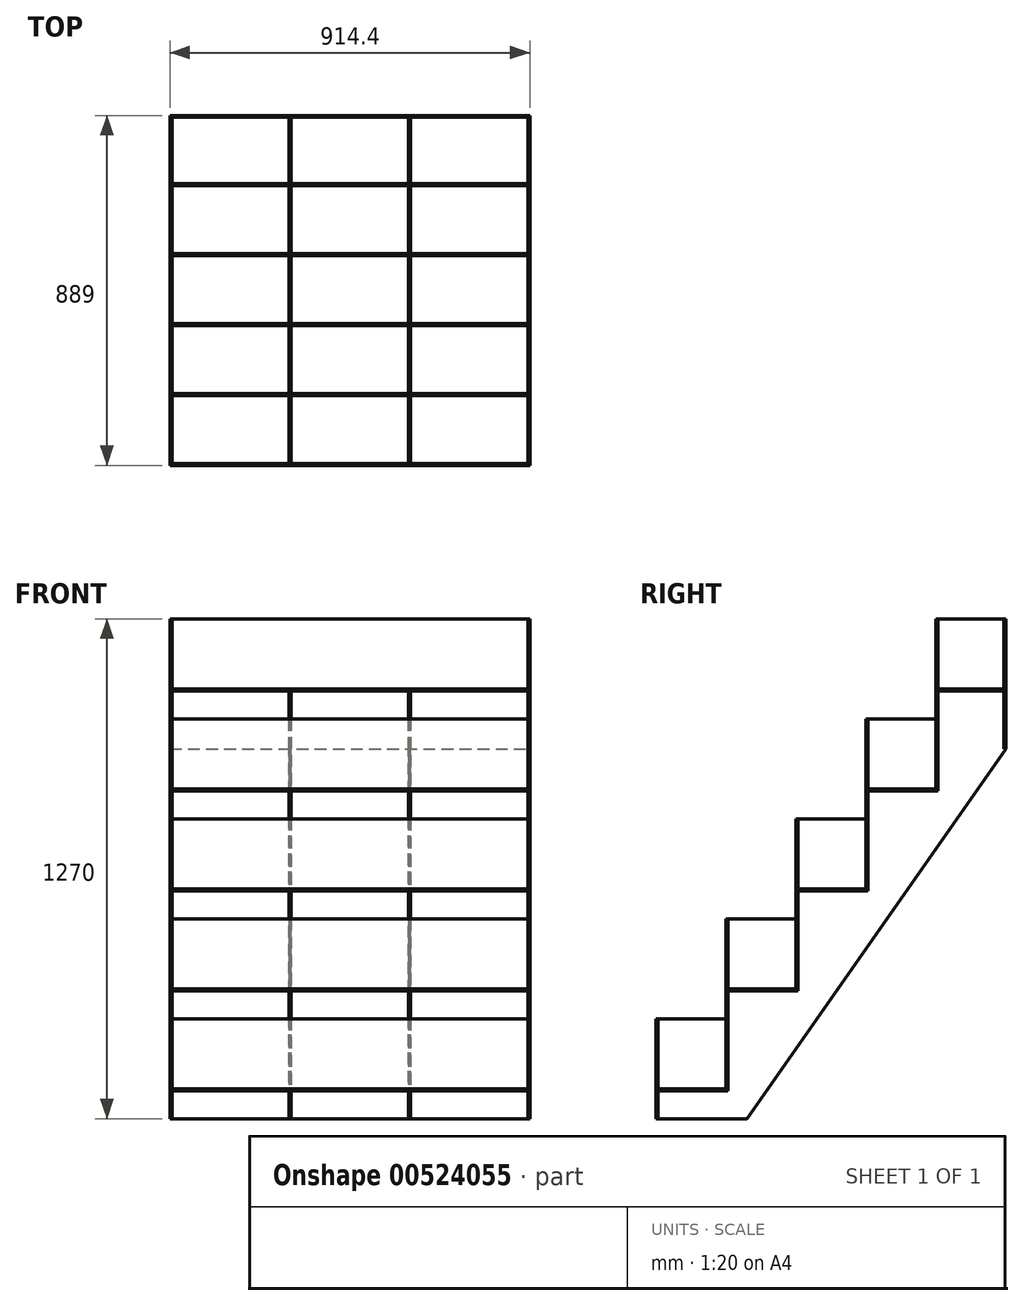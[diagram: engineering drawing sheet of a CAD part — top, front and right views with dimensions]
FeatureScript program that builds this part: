
annotation { "Feature Type Name" : "Feature", "Feature Type Description" : "" }
export const myFeature = defineFeature(function(context is Context, id is Id, definition is map)
    precondition{}
    {
        {
            assignVariable(context, id + "F0", {"name" : "matthick", "anyValue" : 5 * mm});
        }
        {
            var Q0;
            Q0=qCreatedBy(makeId("Right.planeOp"),FACE);
            var sketch = newSketch(context, id + "F1", { "sketchPlane" : qUnion([Q0])});
            skLineSegment(sketch, "E0", {"start": v(-436.82, -657.41) * mm, "end": v(-205.43, -657.41) * mm});
            skLineSegment(sketch, "E1", {"start": v(-205.43, -657.41) * mm, "end": v(452.18, 281.76) * mm});
            skLineSegment(sketch, "E2", {"start": v(452.18, 281.76) * mm, "end": v(452.18, 612.59) * mm});
            skLineSegment(sketch, "E3", {"start": v(452.18, 612.59) * mm, "end": v(274.38, 612.59) * mm});
            skLineSegment(sketch, "E4", {"start": v(274.38, 612.59) * mm, "end": v(274.38, 358.59) * mm});
            skLineSegment(sketch, "E5", {"start": v(274.38, 358.59) * mm, "end": v(96.58, 358.59) * mm});
            skLineSegment(sketch, "E6", {"start": v(96.58, 358.59) * mm, "end": v(96.58, 104.59) * mm});
            skLineSegment(sketch, "E7", {"start": v(96.58, 104.59) * mm, "end": v(-81.22, 104.59) * mm});
            skLineSegment(sketch, "E8", {"start": v(-81.22, 104.59) * mm, "end": v(-81.22, -149.41) * mm});
            skLineSegment(sketch, "E9", {"start": v(-81.22, -149.41) * mm, "end": v(-259.02, -149.41) * mm});
            skLineSegment(sketch, "E10", {"start": v(-259.02, -149.41) * mm, "end": v(-259.02, -403.41) * mm});
            skLineSegment(sketch, "E11", {"start": v(-259.02, -403.41) * mm, "end": v(-436.82, -403.41) * mm});
            skLineSegment(sketch, "E12", {"start": v(-436.82, -403.41) * mm, "end": v(-436.82, -657.41) * mm});
            skSolve(sketch);
        }
        {
            var Q0;
            Q0 = qSketchRegion(id + "F1", true);
            extrude(context, id + "F2", {"entities" : qUnion([Q0]), "depth" : getVariable(context, 'matthick'), "offsetDistance" : 25.4 * mm});
        }
        {
            var Q0;
            Q0=makeQuery(id+"F2.opExtrude","CAP_FACE",FACE,{"disambiguationData":[OSD([sQuery(id+"F1.wireOp",EDGE,"E0"),sQuery(id+"F1.wireOp",EDGE,"E1"),sQuery(id+"F1.wireOp",EDGE,"E2"),sQuery(id+"F1.wireOp",EDGE,"E3"),sQuery(id+"F1.wireOp",EDGE,"E4"),sQuery(id+"F1.wireOp",EDGE,"E5"),sQuery(id+"F1.wireOp",EDGE,"E6"),sQuery(id+"F1.wireOp",EDGE,"E7"),sQuery(id+"F1.wireOp",EDGE,"E8"),sQuery(id+"F1.wireOp",EDGE,"E9"),sQuery(id+"F1.wireOp",EDGE,"E10"),sQuery(id+"F1.wireOp",EDGE,"E11"),sQuery(id+"F1.wireOp",EDGE,"E12")])],"isStart":false});
            var sketch = newSketch(context, id + "F3", { "sketchPlane" : qUnion([Q0])});
            skLineSegment(sketch, "E13", {"start": v(274.38, 612.59) * mm, "end": v(274.38, 434.79) * mm, "construction": true});
            skLineSegment(sketch, "E14.bottom", {"start": v(274.38, 434.79) * mm, "end": v(452.18, 434.79) * mm});
            skLineSegment(sketch, "E14.top", {"start": v(274.38, 429.79) * mm, "end": v(452.18, 429.79) * mm});
            skLineSegment(sketch, "E14.left", {"start": v(274.38, 434.79) * mm, "end": v(274.38, 429.79) * mm});
            skLineSegment(sketch, "E14.right", {"start": v(452.18, 434.79) * mm, "end": v(452.18, 429.79) * mm});
            skSolve(sketch);
        }
        {
            var Q0;
            Q0=makeQuery(id+"F3.imprint","IMPRINT",FACE,{"disambiguationData":[TD([[makeQuery(id+"F3.imprint","IMPRINT",EDGE,{"derivedFrom":sQuery(id+"F3.wireOp",EDGE,"E14.bottom")}),-1.0]])]});
            extrude(context, id + "F4", {"entities" : qUnion([Q0]), "oppositeDirection" : true, "depth" : 914.4 * mm, "offsetDistance" : 25.4 * mm});
        }
        {
            var Q0;
            Q0=makeQuery(id+"F4.opExtrude","SWEPT_BODY",BODY,{"disambiguationData":[OSD([sQuery(id+"F3.wireOp",EDGE,"E14.bottom"),sQuery(id+"F3.wireOp",EDGE,"E14.top"),sQuery(id+"F3.wireOp",EDGE,"E14.left"),sQuery(id+"F3.wireOp",EDGE,"E14.right")])]});
            var Q1;
            Q1=sQuery(id+"F1.wireOp",EDGE,"E4");
            var Q2;
            Q2=sQuery(id+"F1.wireOp",EDGE,"E5");
            transform(context, id + "F5", {"entities" : qUnion([Q0]), "transformType" : TransformType.TRANSLATION_3D, "dx" : 0 * mm, "dy" : -177.8 * mm, "dz" : -254 * mm, "makeCopy" : true});
        }
        {
            var Q0;
            Q0=makeQuery(id+"F2.opExtrude","CAP_FACE",FACE,{"disambiguationData":[OSD([sQuery(id+"F1.wireOp",EDGE,"E0"),sQuery(id+"F1.wireOp",EDGE,"E1"),sQuery(id+"F1.wireOp",EDGE,"E2"),sQuery(id+"F1.wireOp",EDGE,"E3"),sQuery(id+"F1.wireOp",EDGE,"E4"),sQuery(id+"F1.wireOp",EDGE,"E5"),sQuery(id+"F1.wireOp",EDGE,"E6"),sQuery(id+"F1.wireOp",EDGE,"E7"),sQuery(id+"F1.wireOp",EDGE,"E8"),sQuery(id+"F1.wireOp",EDGE,"E9"),sQuery(id+"F1.wireOp",EDGE,"E10"),sQuery(id+"F1.wireOp",EDGE,"E11"),sQuery(id+"F1.wireOp",EDGE,"E12")])],"isStart":false});
            var sketch = newSketch(context, id + "F6", { "sketchPlane" : qUnion([Q0])});
            skLineSegment(sketch, "E15.bottom", {"start": v(274.38, 612.59) * mm, "end": v(279.38, 612.59) * mm});
            skLineSegment(sketch, "E15.top", {"start": v(274.38, 175.79) * mm, "end": v(279.38, 175.79) * mm});
            skLineSegment(sketch, "E15.left", {"start": v(274.38, 612.59) * mm, "end": v(274.38, 175.79) * mm});
            skLineSegment(sketch, "E15.right", {"start": v(279.38, 612.59) * mm, "end": v(279.38, 175.79) * mm});
            skSolve(sketch);
        }
        {
            var Q0;
            Q0 = qSketchRegion(id + "F6", true);
            extrude(context, id + "F7", {"entities" : qUnion([Q0]), "oppositeDirection" : true, "depth" : 914.4 * mm, "offsetDistance" : 25.4 * mm});
        }
        {
            var Q0;
            Q0=makeQuery(id+"F5.opPattern","COPY",BODY,{"derivedFrom":makeQuery(id+"F4.opExtrude","SWEPT_BODY",BODY,{"disambiguationData":[OSD([sQuery(id+"F3.wireOp",EDGE,"E14.bottom"),sQuery(id+"F3.wireOp",EDGE,"E14.top"),sQuery(id+"F3.wireOp",EDGE,"E14.left"),sQuery(id+"F3.wireOp",EDGE,"E14.right")])]}),"instanceName":"1"});
            var Q1;
            Q1=makeQuery(id+"F7.opExtrude","SWEPT_BODY",BODY,{"disambiguationData":[OSD([sQuery(id+"F6.wireOp",EDGE,"E15.bottom"),sQuery(id+"F6.wireOp",EDGE,"E15.top"),sQuery(id+"F6.wireOp",EDGE,"E15.left"),sQuery(id+"F6.wireOp",EDGE,"E15.right")])]});
            transform(context, id + "F8", {"entities" : qUnion([Q0, Q1]), "transformType" : TransformType.TRANSLATION_3D, "dx" : 0 * mm, "dy" : -177.8 * mm, "dz" : -254 * mm, "makeCopy" : true});
        }
        {
            var Q0;
            Q0=makeQuery(id+"F8.opPattern","COPY",BODY,{"derivedFrom":makeQuery(id+"F5.opPattern","COPY",BODY,{"derivedFrom":makeQuery(id+"F4.opExtrude","SWEPT_BODY",BODY,{"disambiguationData":[OSD([sQuery(id+"F3.wireOp",EDGE,"E14.bottom"),sQuery(id+"F3.wireOp",EDGE,"E14.top"),sQuery(id+"F3.wireOp",EDGE,"E14.left"),sQuery(id+"F3.wireOp",EDGE,"E14.right")])]}),"instanceName":"1"}),"instanceName":"1"});
            var Q1;
            Q1=makeQuery(id+"F8.opPattern","COPY",BODY,{"derivedFrom":makeQuery(id+"F7.opExtrude","SWEPT_BODY",BODY,{"disambiguationData":[OSD([sQuery(id+"F6.wireOp",EDGE,"E15.bottom"),sQuery(id+"F6.wireOp",EDGE,"E15.top"),sQuery(id+"F6.wireOp",EDGE,"E15.left"),sQuery(id+"F6.wireOp",EDGE,"E15.right")])]}),"instanceName":"1"});
            transform(context, id + "F9", {"entities" : qUnion([Q0, Q1]), "transformType" : TransformType.TRANSLATION_3D, "dx" : 0 * mm, "dy" : -177.8 * mm, "dz" : -254 * mm, "makeCopy" : true});
        }
        {
            var Q0;
            Q0=makeQuery(id+"F9.opPattern","COPY",BODY,{"derivedFrom":makeQuery(id+"F8.opPattern","COPY",BODY,{"derivedFrom":makeQuery(id+"F5.opPattern","COPY",BODY,{"derivedFrom":makeQuery(id+"F4.opExtrude","SWEPT_BODY",BODY,{"disambiguationData":[OSD([sQuery(id+"F3.wireOp",EDGE,"E14.bottom"),sQuery(id+"F3.wireOp",EDGE,"E14.top"),sQuery(id+"F3.wireOp",EDGE,"E14.left"),sQuery(id+"F3.wireOp",EDGE,"E14.right")])]}),"instanceName":"1"}),"instanceName":"1"}),"instanceName":"1"});
            var Q1;
            Q1=makeQuery(id+"F9.opPattern","COPY",BODY,{"derivedFrom":makeQuery(id+"F8.opPattern","COPY",BODY,{"derivedFrom":makeQuery(id+"F7.opExtrude","SWEPT_BODY",BODY,{"disambiguationData":[OSD([sQuery(id+"F6.wireOp",EDGE,"E15.bottom"),sQuery(id+"F6.wireOp",EDGE,"E15.top"),sQuery(id+"F6.wireOp",EDGE,"E15.left"),sQuery(id+"F6.wireOp",EDGE,"E15.right")])]}),"instanceName":"1"}),"instanceName":"1"});
            transform(context, id + "F10", {"entities" : qUnion([Q0, Q1]), "transformType" : TransformType.TRANSLATION_3D, "dx" : 0 * mm, "dy" : -177.8 * mm, "dz" : -254 * mm, "makeCopy" : true});
        }
        {
            var Q0;
            Q0=makeQuery(id+"F2.opExtrude","SWEPT_BODY",BODY,{"disambiguationData":[OSD([sQuery(id+"F1.wireOp",EDGE,"E0"),sQuery(id+"F1.wireOp",EDGE,"E1"),sQuery(id+"F1.wireOp",EDGE,"E2"),sQuery(id+"F1.wireOp",EDGE,"E3"),sQuery(id+"F1.wireOp",EDGE,"E4"),sQuery(id+"F1.wireOp",EDGE,"E5"),sQuery(id+"F1.wireOp",EDGE,"E6"),sQuery(id+"F1.wireOp",EDGE,"E7"),sQuery(id+"F1.wireOp",EDGE,"E8"),sQuery(id+"F1.wireOp",EDGE,"E9"),sQuery(id+"F1.wireOp",EDGE,"E10"),sQuery(id+"F1.wireOp",EDGE,"E11"),sQuery(id+"F1.wireOp",EDGE,"E12")])]});
            var Q1;
            Q1=makeQuery(id+"F7.opExtrude","SWEPT_EDGE",EDGE,{"disambiguationData":[OSD([sQuery(id+"F6.wireOp",EDGE,"E15.bottom"),sQuery(id+"F6.wireOp",EDGE,"E15.left")])]});
            transform(context, id + "F11", {"entities" : qUnion([Q0]), "transformType" : TransformType.TRANSLATION_3D, "dx" : -914.4 * mm + getVariable(context, 'matthick'), "dy" : 0 * mm, "dz" : 0 * mm, "makeCopy" : true});
        }
        {
            var Q0;
            Q0=makeQuery(id+"F2.opExtrude","CAP_FACE",FACE,{"disambiguationData":[OSD([sQuery(id+"F1.wireOp",EDGE,"E0"),sQuery(id+"F1.wireOp",EDGE,"E1"),sQuery(id+"F1.wireOp",EDGE,"E2"),sQuery(id+"F1.wireOp",EDGE,"E3"),sQuery(id+"F1.wireOp",EDGE,"E4"),sQuery(id+"F1.wireOp",EDGE,"E5"),sQuery(id+"F1.wireOp",EDGE,"E6"),sQuery(id+"F1.wireOp",EDGE,"E7"),sQuery(id+"F1.wireOp",EDGE,"E8"),sQuery(id+"F1.wireOp",EDGE,"E9"),sQuery(id+"F1.wireOp",EDGE,"E10"),sQuery(id+"F1.wireOp",EDGE,"E11"),sQuery(id+"F1.wireOp",EDGE,"E12")])],"isStart":false});
            var sketch = newSketch(context, id + "F12", { "sketchPlane" : qUnion([Q0])});
            skLineSegment(sketch, "E16.bottom", {"start": v(-436.82, -403.41) * mm, "end": v(-431.82, -403.41) * mm});
            skLineSegment(sketch, "E16.top", {"start": v(-436.82, -657.41) * mm, "end": v(-431.82, -657.41) * mm});
            skLineSegment(sketch, "E16.left", {"start": v(-436.82, -403.41) * mm, "end": v(-436.82, -657.41) * mm});
            skLineSegment(sketch, "E16.right", {"start": v(-431.82, -403.41) * mm, "end": v(-431.82, -657.41) * mm});
            skSolve(sketch);
        }
        {
            var Q0;
            Q0 = qSketchRegion(id + "F12", true);
            extrude(context, id + "F13", {"entities" : qUnion([Q0]), "oppositeDirection" : true, "depth" : 914.4 * mm, "offsetDistance" : 25.4 * mm});
        }
        {
            var Q0;
            Q0=makeQuery(id+"F2.opExtrude","CAP_FACE",FACE,{"disambiguationData":[OSD([sQuery(id+"F1.wireOp",EDGE,"E0"),sQuery(id+"F1.wireOp",EDGE,"E1"),sQuery(id+"F1.wireOp",EDGE,"E2"),sQuery(id+"F1.wireOp",EDGE,"E3"),sQuery(id+"F1.wireOp",EDGE,"E4"),sQuery(id+"F1.wireOp",EDGE,"E5"),sQuery(id+"F1.wireOp",EDGE,"E6"),sQuery(id+"F1.wireOp",EDGE,"E7"),sQuery(id+"F1.wireOp",EDGE,"E8"),sQuery(id+"F1.wireOp",EDGE,"E9"),sQuery(id+"F1.wireOp",EDGE,"E10"),sQuery(id+"F1.wireOp",EDGE,"E11"),sQuery(id+"F1.wireOp",EDGE,"E12")])],"isStart":false});
            var sketch = newSketch(context, id + "F14", { "sketchPlane" : qUnion([Q0])});
            skLineSegment(sketch, "E17.bottom", {"start": v(452.18, 612.59) * mm, "end": v(447.18, 612.59) * mm});
            skLineSegment(sketch, "E17.top", {"start": v(452.18, 281.76) * mm, "end": v(447.18, 281.76) * mm});
            skLineSegment(sketch, "E17.left", {"start": v(452.18, 612.59) * mm, "end": v(452.18, 281.76) * mm});
            skLineSegment(sketch, "E17.right", {"start": v(447.18, 612.59) * mm, "end": v(447.18, 281.76) * mm});
            skSolve(sketch);
        }
        {
            var Q0;
            Q0 = qSketchRegion(id + "F14", true);
            extrude(context, id + "F15", {"entities" : qUnion([Q0]), "oppositeDirection" : true, "depth" : 914.4 * mm, "offsetDistance" : 25.4 * mm});
        }
        {
            var Q0;
            Q0=makeQuery(id+"F2.opExtrude","CAP_FACE",FACE,{"disambiguationData":[OSD([sQuery(id+"F1.wireOp",EDGE,"E0"),sQuery(id+"F1.wireOp",EDGE,"E1"),sQuery(id+"F1.wireOp",EDGE,"E2"),sQuery(id+"F1.wireOp",EDGE,"E3"),sQuery(id+"F1.wireOp",EDGE,"E4"),sQuery(id+"F1.wireOp",EDGE,"E5"),sQuery(id+"F1.wireOp",EDGE,"E6"),sQuery(id+"F1.wireOp",EDGE,"E7"),sQuery(id+"F1.wireOp",EDGE,"E8"),sQuery(id+"F1.wireOp",EDGE,"E9"),sQuery(id+"F1.wireOp",EDGE,"E10"),sQuery(id+"F1.wireOp",EDGE,"E11"),sQuery(id+"F1.wireOp",EDGE,"E12")])],"isStart":false});
            var sketch = newSketch(context, id + "F16", { "sketchPlane" : qUnion([Q0])});
            skLineSegment(sketch, "E18", {"start": v(-436.82, -657.41) * mm, "end": v(-205.43, -657.41) * mm});
            skLineSegment(sketch, "E19", {"start": v(-205.43, -657.41) * mm, "end": v(452.18, 281.76) * mm});
            skLineSegment(sketch, "E20", {"start": v(452.18, 281.76) * mm, "end": v(452.18, 434.79) * mm});
            skLineSegment(sketch, "E21", {"start": v(452.18, 434.79) * mm, "end": v(274.38, 434.79) * mm});
            skLineSegment(sketch, "E22", {"start": v(274.38, 434.79) * mm, "end": v(274.38, 180.79) * mm});
            skLineSegment(sketch, "E23", {"start": v(274.38, 180.79) * mm, "end": v(96.58, 180.79) * mm});
            skLineSegment(sketch, "E24", {"start": v(96.58, 180.79) * mm, "end": v(96.58, -73.21) * mm});
            skLineSegment(sketch, "E25", {"start": v(96.58, -73.21) * mm, "end": v(-81.22, -73.21) * mm});
            skLineSegment(sketch, "E26", {"start": v(-81.22, -73.21) * mm, "end": v(-81.22, -327.21) * mm});
            skLineSegment(sketch, "E27", {"start": v(-81.22, -327.21) * mm, "end": v(-259.02, -327.21) * mm});
            skLineSegment(sketch, "E28", {"start": v(-259.02, -327.21) * mm, "end": v(-259.02, -581.21) * mm});
            skLineSegment(sketch, "E29", {"start": v(-259.02, -581.21) * mm, "end": v(-436.82, -581.21) * mm});
            skLineSegment(sketch, "E30", {"start": v(-436.82, -581.21) * mm, "end": v(-436.82, -657.41) * mm});
            skSolve(sketch);
        }
        {
            var Q0;
            Q0=makeQuery(id+"F16.imprint","IMPRINT",FACE,{"disambiguationData":[TD([[makeQuery(id+"F16.imprint","IMPRINT",EDGE,{"derivedFrom":sQuery(id+"F16.wireOp",EDGE,"E19")}),1.0]])]});
            extrude(context, id + "F17", {"entities" : qUnion([Q0]), "oppositeDirection" : true, "depth" : getVariable(context, 'matthick'), "offsetDistance" : 25.4 * mm});
        }
        {
            var Q0;
            Q0=makeQuery(id+"F17.opExtrude","SWEPT_BODY",BODY,{"disambiguationData":[OSD([sQuery(id+"F1.wireOp",EDGE,"E0"),sQuery(id+"F16.wireOp",EDGE,"E19"),sQuery(id+"F16.wireOp",EDGE,"E20"),sQuery(id+"F16.wireOp",EDGE,"E21"),sQuery(id+"F16.wireOp",EDGE,"E22"),sQuery(id+"F16.wireOp",EDGE,"E23"),sQuery(id+"F16.wireOp",EDGE,"E24"),sQuery(id+"F16.wireOp",EDGE,"E25"),sQuery(id+"F16.wireOp",EDGE,"E26"),sQuery(id+"F16.wireOp",EDGE,"E27"),sQuery(id+"F16.wireOp",EDGE,"E28"),sQuery(id+"F16.wireOp",EDGE,"E29"),sQuery(id+"F16.wireOp",EDGE,"E30")])]});
            transform(context, id + "F18", {"entities" : qUnion([Q0]), "transformType" : TransformType.TRANSLATION_3D, "dx" : -304.8 * mm + getVariable(context, 'matthick') * .3333, "dy" : 0 * mm, "dz" : 0 * mm, "makeCopy" : false});
        }
        {
            var Q0;
            Q0=makeQuery(id+"F17.opExtrude","SWEPT_BODY",BODY,{"disambiguationData":[OSD([sQuery(id+"F1.wireOp",EDGE,"E0"),sQuery(id+"F16.wireOp",EDGE,"E19"),sQuery(id+"F16.wireOp",EDGE,"E20"),sQuery(id+"F16.wireOp",EDGE,"E21"),sQuery(id+"F16.wireOp",EDGE,"E22"),sQuery(id+"F16.wireOp",EDGE,"E23"),sQuery(id+"F16.wireOp",EDGE,"E24"),sQuery(id+"F16.wireOp",EDGE,"E25"),sQuery(id+"F16.wireOp",EDGE,"E26"),sQuery(id+"F16.wireOp",EDGE,"E27"),sQuery(id+"F16.wireOp",EDGE,"E28"),sQuery(id+"F16.wireOp",EDGE,"E29"),sQuery(id+"F16.wireOp",EDGE,"E30")])]});
            transform(context, id + "F19", {"entities" : qUnion([Q0]), "transformType" : TransformType.TRANSLATION_3D, "dx" : -304.8 * mm + getVariable(context, 'matthick') * .3333, "dy" : 0 * mm, "dz" : 0 * mm, "makeCopy" : true});
        }
    });
